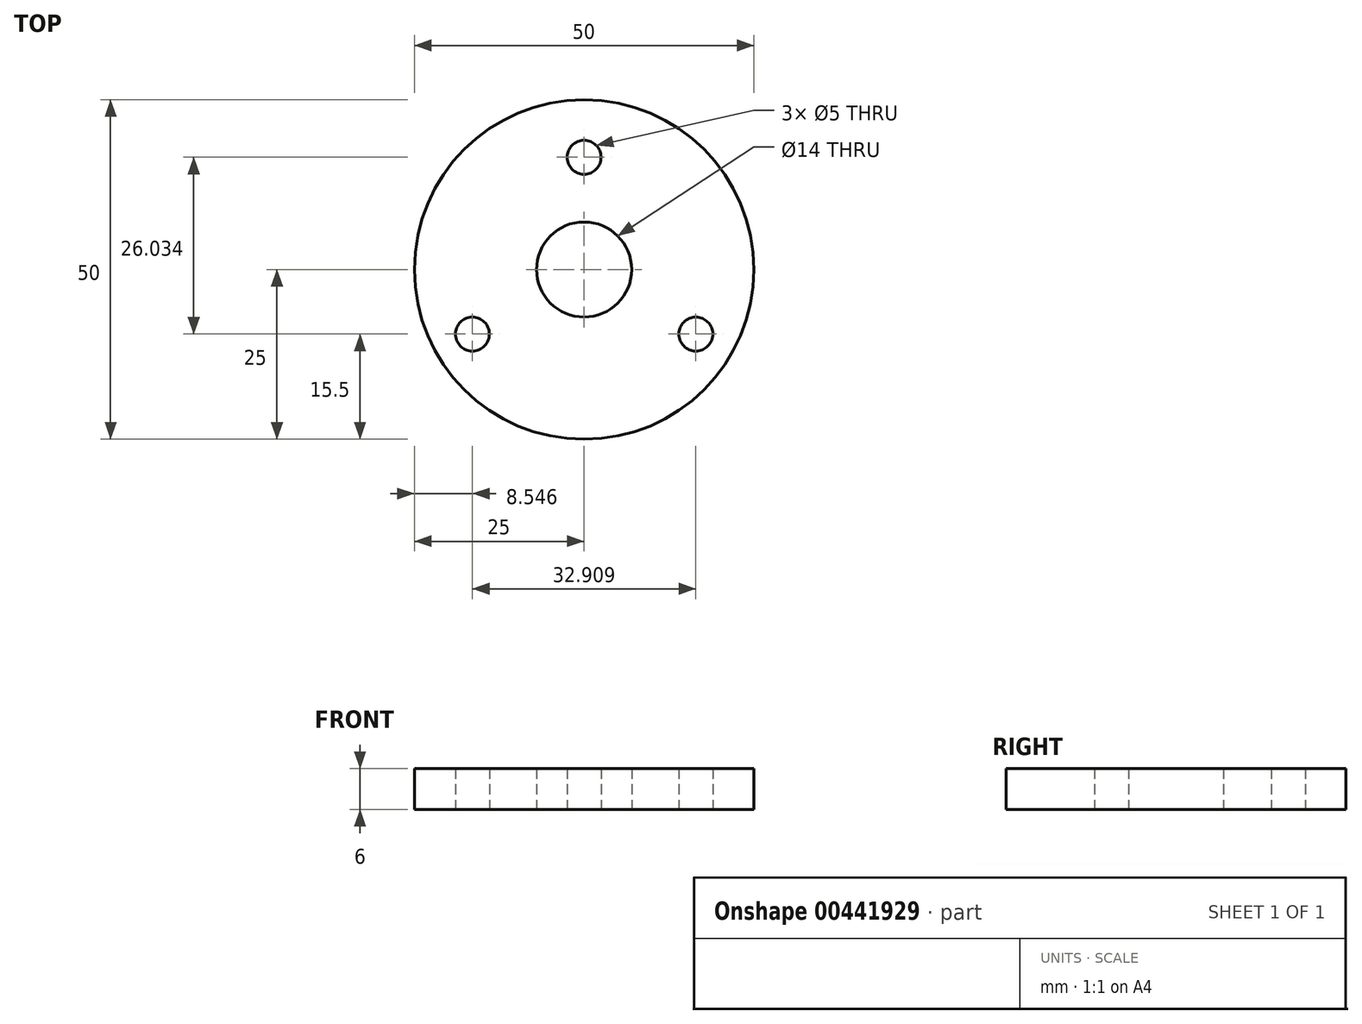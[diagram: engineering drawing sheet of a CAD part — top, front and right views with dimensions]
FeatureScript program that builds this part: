
annotation { "Feature Type Name" : "Feature", "Feature Type Description" : "" }
export const myFeature = defineFeature(function(context is Context, id is Id, definition is map)
    precondition{}
    {
        {
            var Q0;
            Q0=qCreatedBy(makeId("Top.planeOp"),FACE);
            var sketch = newSketch(context, id + "F0", { "sketchPlane" : qUnion([Q0])});
            skCircle(sketch, "E0", {"center": v(0, 0) * mm, "radius": 25 * mm});
            skCircle(sketch, "E1", {"center": v(0, 0) * mm, "radius": 7 * mm});
            skCircle(sketch, "E2", {"center": v(0, 16.53) * mm, "radius": 2.5 * mm});
            skCircle(sketch, "E3", {"center": v(-16.45, -9.5) * mm, "radius": 2.5 * mm});
            skCircle(sketch, "E4", {"center": v(16.45, -9.5) * mm, "radius": 2.5 * mm});
            skSolve(sketch);
        }
        {
            var Q0;
            Q0=makeQuery(id+"F0.imprint","IMPRINT",FACE,{"disambiguationData":[TD([[makeQuery(id+"F0.imprint","IMPRINT",EDGE,{"derivedFrom":sQuery(id+"F0.wireOp",EDGE,"E0")}),1.0]])]});
            extrude(context, id + "F1", {"entities" : qUnion([Q0]), "depth" : 6 * mm});
        }
    });
